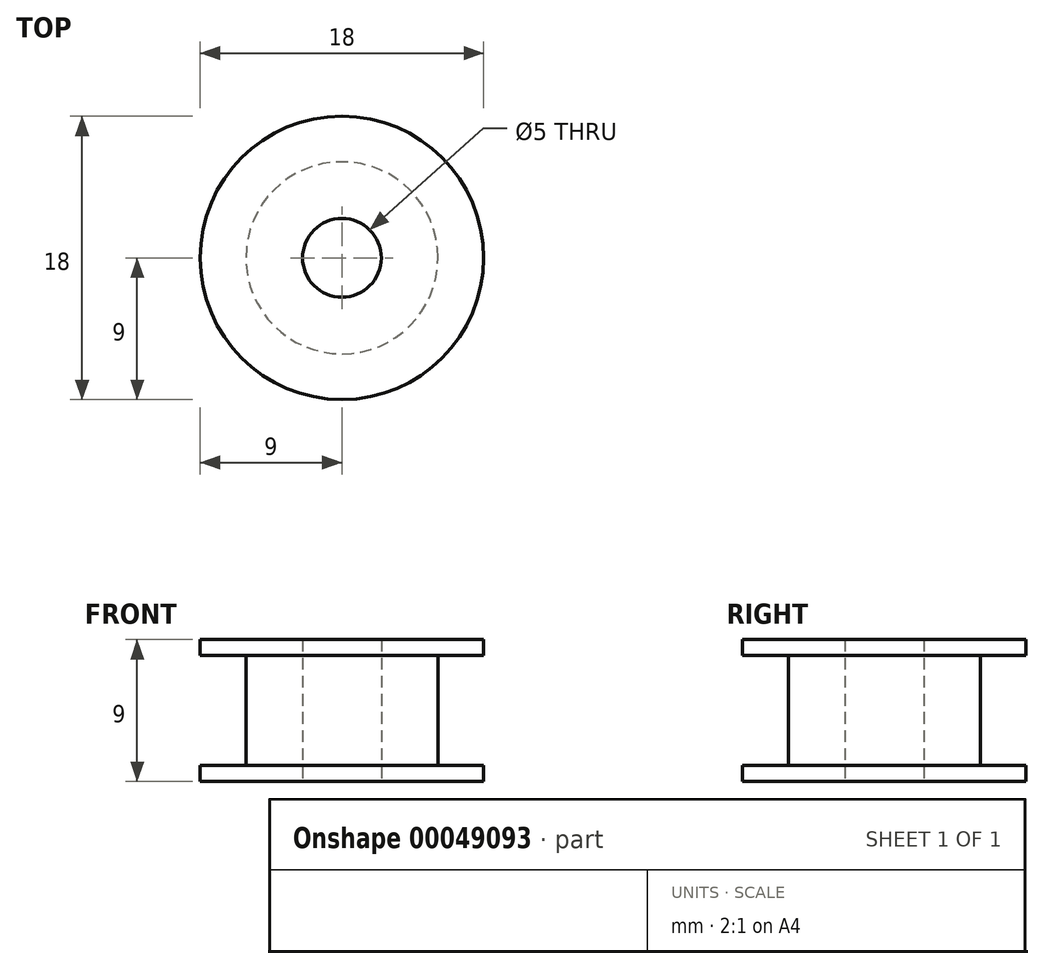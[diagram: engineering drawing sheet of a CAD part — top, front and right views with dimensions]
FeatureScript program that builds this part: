
annotation { "Feature Type Name" : "Feature", "Feature Type Description" : "" }
export const myFeature = defineFeature(function(context is Context, id is Id, definition is map)
    precondition{}
    {
        {
            var Q0;
            Q0=qCreatedBy(makeId("Front.planeOp"),FACE);
            var sketch = newSketch(context, id + "F0", { "sketchPlane" : qUnion([Q0])});
            skLineSegment(sketch, "E0.left", {"start": v(0, 0) * mm, "end": v(0, 9) * mm, "construction": true});
            skLineSegment(sketch, "E1", {"start": v(9, 9) * mm, "end": v(9, 8) * mm});
            skLineSegment(sketch, "E2", {"start": v(9, 8) * mm, "end": v(6.1, 8) * mm});
            skLineSegment(sketch, "E3", {"start": v(6.1, 8) * mm, "end": v(6.1, 1) * mm});
            skLineSegment(sketch, "E4", {"start": v(6.1, 1) * mm, "end": v(9, 1) * mm});
            skLineSegment(sketch, "E5", {"start": v(9, 1) * mm, "end": v(9, 0) * mm});
            skLineSegment(sketch, "E6", {"start": v(2.5, 9) * mm, "end": v(9, 9) * mm});
            skLineSegment(sketch, "E7", {"start": v(2.5, 0) * mm, "end": v(9, 0) * mm});
            skLineSegment(sketch, "E8", {"start": v(2.5, 9) * mm, "end": v(2.5, 0) * mm});
            skSolve(sketch);
        }
        {
            var Q0;
            Q0=makeQuery(id+"F0.imprint","IMPRINT",FACE,{"disambiguationData":[TD([[makeQuery(id+"F0.imprint","IMPRINT",EDGE,{"derivedFrom":sQuery(id+"F0.wireOp",EDGE,"E1")}),-1.0]])]});
            var Q1;
            Q1=sQuery(id+"F0.wireOp",EDGE,"E0.left");
            revolve(context, id + "F1", {"entities" : qUnion([Q0]), "axis" : qUnion([Q1]), "revolveType" : RevolveType.FULL});
        }
    });
